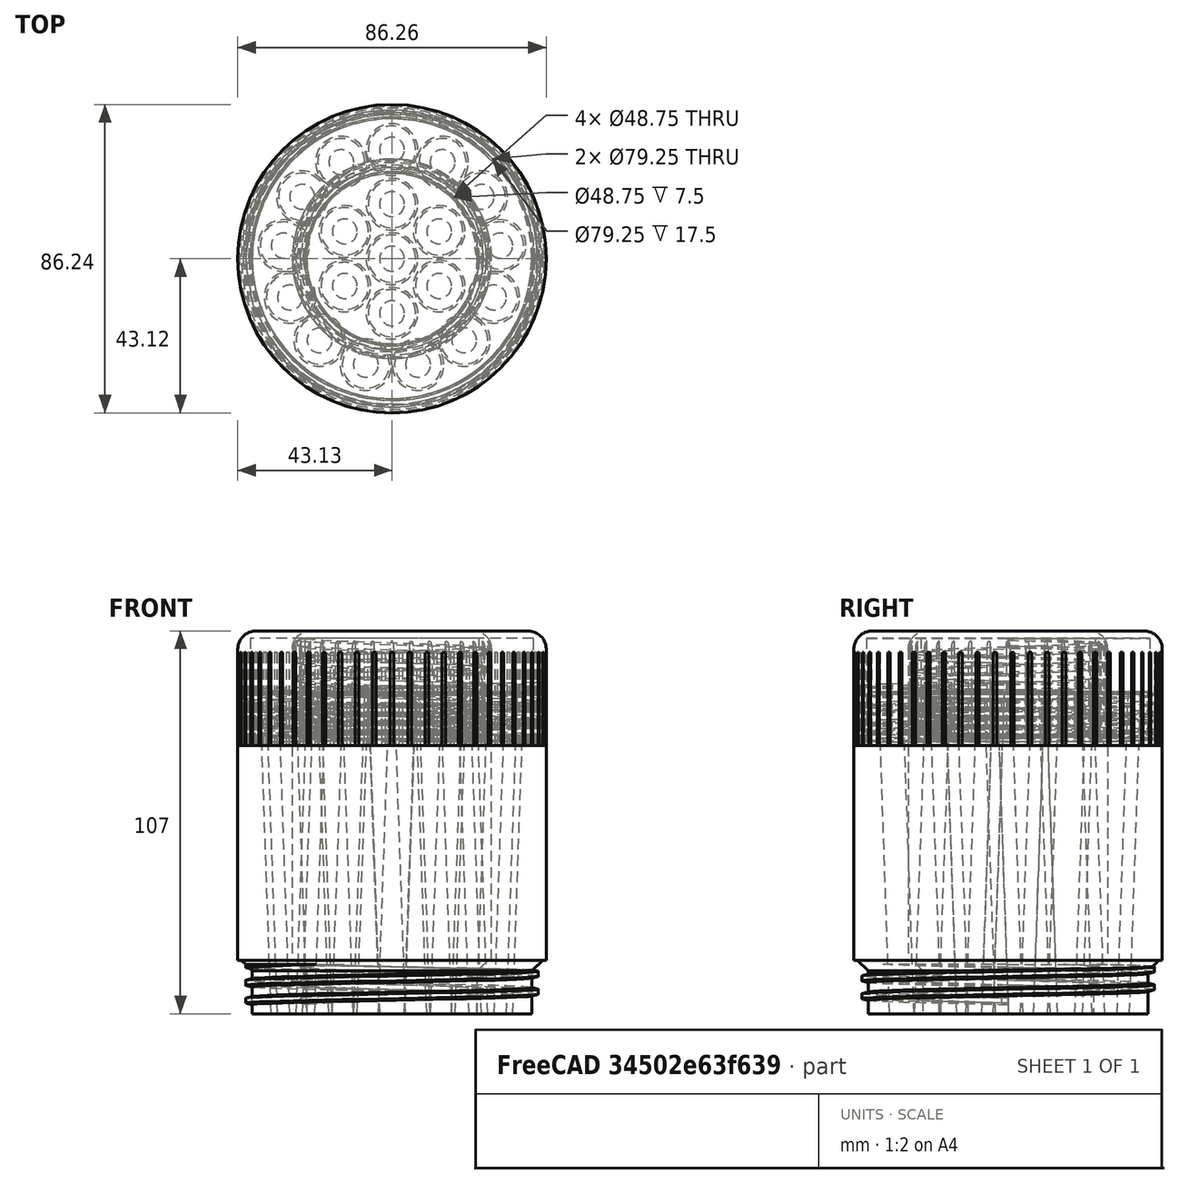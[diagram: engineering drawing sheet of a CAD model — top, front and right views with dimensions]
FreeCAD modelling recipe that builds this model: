
FCSTD DOCUMENT  (FreeCAD 2023.131R26244 +5365 (Git))
Label: Joint Holder
License: All rights reserved
LicenseURL: http://en.wikipedia.org/wiki/All_rights_reserved
objects: Sketcher::SketchObject×23, PartDesign::Pocket×13, PartDesign::Chamfer×6, PartDesign::PolarPattern×5, PartDesign::Pad×4, PartDesign::AdditiveHelix×4, PartDesign::Body×4, PartDesign::SubtractiveHelix×2, PartDesign::Fillet×2, Spreadsheet::Sheet×1
note: 158 computed .brp shape members not serialized (recipe doc carries the construction recipe); baked Part::Feature solids carry a one-line shape summary decoded from their .brp

FEATURE [Spreadsheet::Sheet] Spreadsheet  label="Parameters"
  PythonMode = false
  ShowCells = 0
  TreeRank = 1
  cells = A1=Thickness; B1(Thickness)=2; A2=Seven Cone Diameter; B2(small_holder_diameter)==Cone_Offset * 3 + Thickness * 5; D2=<-- Calculated; F2==large_holder_diameter / small_holder_diameter; A3=Twenty Holder Diameter; B3(large_holder_diameter)==Cone_Offset * 5 + Thickness * 5; D3=<-- Calculated; A4=Body Height; B4(body_height)=90; A5=Shoulder Height; B5(shoulder_height)=15; A6=Shoulder Depth; B6(shoulder_depth)==Thickness * 2; D6=<-- Calculated; A7=Cap Recess; B7(cap_recess)=15; A9=Cone Max Diameter; B9(Cone_Diameter_Max)=13.25; A10=Cone Min Diameter; B10(Cone_Diameter_Min)=6; A11=Cone Length; B11(Cone_Length)=110; A12=Cone Angle; B12(Cone_Angle)=2; E12==asin((Cone_Diameter_Max - Cone_Diameter_Min) / Cone_Length); A13=Cone Offset; B13(Cone_Offset)==Cone_Diameter_Max + Thickness; D13=<-- Calculated; A14=1st Cone Ring Count; B14(Cone_1st_Ring_Count)=6; A15=2nd Cone Ring Count; B15(Cone_2nd_Ring_Count)=13; A17=Tooth Depth; B17(tooth_depth)=2; A18=Thread Pitch; B18(thread_pitch)=2.5; A19=Thread Angle; B19(thread_angle)=15; A20=Thread Depth; B20(thread_depth)=2; A21=Thread Clearance; B21(thread_clearance)==thread_depth / 10
FEATURE [Sketcher::SketchObject] Sketch
  ArcFitTolerance = 1e-06
  AttachmentSupport = -> [XY_Plane]
  ExternalBSplineMaxDegree = 5
  ExternalBSplineTolerance = 0.0001
  FullyConstrained = true
  InternalTolerance = 1e-06
  InvalidShape = false
  MakeInternals = false
  MapMode = 5
  Support = -> [XY_Plane]
  TreeRank = 12
  ValidateShape = true
  expr: Constraints[1] = Spreadsheet.small_holder_diameter
  sketch-geometry (1):
    g0: Circle CenterX=0 CenterY=0 CenterZ=0 NormalX=0 NormalY=0 NormalZ=1 AngleXU=0 Radius=27.875
  constraints (2):
    c: Coincident(g0,g-1)
    c: Diameter(g0) = 55.75
FEATURE [PartDesign::Pad] Pad  label="Small Body"
  AddSubType = 0
  AlongSketchNormal = false
  AutoTaperInnerAngle = true
  CheckUpToFaceLimits = true
  ClaimChildren = false
  Direction = (0,0,1)
  Fit = 0
  FitJoin = 0
  InnerFit = 0
  InnerFitJoin = 0
  InvalidShape = false
  Length = 15
  Length2 = 75
  Linearize = true
  NewSolid = false
  Profile = -> Sketch
  Suppress = false
  TaperInnerAngle = 0
  TaperInnerAngleRev = 0
  TreeRank = 13
  Type = 4
  ValidateShape = true
  _ProfileBasedVersion = 1
  expr: Length = <<Parameters>>.shoulder_height
  expr: Length2 = <<Parameters>>.body_height - <<Parameters>>.shoulder_height
FEATURE [Sketcher::SketchObject] Sketch001
  ArcFitTolerance = 1e-06
  AttachmentSupport = -> [Pad]
  ExternalBSplineMaxDegree = 5
  ExternalBSplineTolerance = 0.0001
  FullyConstrained = true
  InternalTolerance = 1e-06
  InvalidShape = false
  MakeInternals = false
  MapMode = 5
  Placement = pos=(0,0,15) rot=(0,0,1;0rad)
  Support = -> [Pad]
  TreeRank = 14
  ValidateShape = true
  expr: Constraints[1] = <<Parameters>>.Cone_Diameter_Max
  sketch-geometry (1):
    g0: Circle CenterX=0 CenterY=0 CenterZ=0 NormalX=0 NormalY=0 NormalZ=1 AngleXU=0 Radius=6.625
  constraints (2):
    c: Coincident(g0,g-1)
    c: Diameter(g0) = 13.25
FEATURE [PartDesign::Pocket] Pocket  label="Small Middle Cone"
  AddSubType = 1
  AutoTaperInnerAngle = true
  BaseFeature = -> Pad
  CheckUpToFaceLimits = true
  ClaimChildren = false
  Fit = 0
  FitJoin = 0
  InnerFit = 0
  InnerFitJoin = 0
  InvalidShape = false
  Length = 110
  Length2 = 100
  Linearize = true
  NewSolid = false
  Profile = -> Sketch001
  Suppress = false
  TaperAngle = -2
  TaperInnerAngle = 2
  TaperInnerAngleRev = 0
  TreeRank = 15
  Type = 0
  ValidateShape = true
  _ProfileBasedVersion = 1
  _Version = 1
  expr: Length = <<Parameters>>.Cone_Length
  expr: TaperAngle = -<<Parameters>>.Cone_Angle
FEATURE [Sketcher::SketchObject] Sketch002
  ArcFitTolerance = 1e-06
  AttachmentSupport = -> [Pocket]
  ExternalBSplineMaxDegree = 5
  ExternalBSplineTolerance = 0.0001
  FullyConstrained = true
  InternalTolerance = 1e-06
  InvalidShape = false
  MakeInternals = false
  MapMode = 5
  Placement = pos=(0,0,15) rot=(0,0,1;0rad)
  Support = -> [Pocket]
  TreeRank = 16
  ValidateShape = true
  expr: Constraints[1] = <<Parameters>>.Cone_Diameter_Max
  expr: Constraints[2] = <<Parameters>>.Cone_Offset
  sketch-geometry (1):
    g0: Circle CenterX=0 CenterY=15.25 CenterZ=0 NormalX=0 NormalY=0 NormalZ=1 AngleXU=0 Radius=6.625
  constraints (3):
    c: PointOnObject(g0,g-2)
    c: Diameter(g0) = 13.25
    c: DistanceY(g-1,g0) = 15.25
FEATURE [PartDesign::Pocket] Pocket001  label="Small Outer Cone"
  AddSubType = 1
  AutoTaperInnerAngle = true
  BaseFeature = -> Pocket
  CheckUpToFaceLimits = true
  ClaimChildren = false
  Fit = 0
  FitJoin = 0
  InnerFit = 0
  InnerFitJoin = 0
  InvalidShape = false
  Length = 110
  Length2 = 100
  Linearize = true
  NewSolid = false
  Profile = -> Sketch002
  Suppress = false
  TaperAngle = -2
  TaperInnerAngle = 2
  TaperInnerAngleRev = 0
  TreeRank = 17
  Type = 0
  ValidateShape = true
  _ProfileBasedVersion = 1
  _Version = 1
  expr: Length = <<Parameters>>.Cone_Length
  expr: TaperAngle = -<<Parameters>>.Cone_Angle
FEATURE [PartDesign::PolarPattern] PolarPattern  label="Small Outer Cone Ring"
  AddSubType = 0
  Angle = 360
  Axis = -> Sketch002 [N_Axis]
  BaseFeature = -> Pocket001
  CopyShape = false
  InvalidShape = false
  NewSolid = false
  Occurrences = 6
  OriginalSubs = -> [Pocket001]
  Originals = -> [Pocket001]
  ParallelTransform = true
  SubTransform = true
  Suppress = false
  TreeRank = 18
  ValidateShape = true
  _Version = 3
  expr: Occurrences = <<Parameters>>.Cone_1st_Ring_Count
FEATURE [Sketcher::SketchObject] Sketch003
  ArcFitTolerance = 1e-06
  AttachmentSupport = -> [XY_Plane001]
  ExternalBSplineMaxDegree = 5
  ExternalBSplineTolerance = 0.0001
  FullyConstrained = true
  InternalTolerance = 1e-06
  InvalidShape = false
  MakeInternals = false
  MapMode = 5
  Support = -> [XY_Plane001]
  TreeRank = 29
  ValidateShape = true
  expr: Constraints[1] = <<Parameters>>.large_holder_diameter
  sketch-geometry (1):
    g0: Circle CenterX=0 CenterY=0 CenterZ=0 NormalX=0 NormalY=0 NormalZ=1 AngleXU=0 Radius=43.125
  constraints (2):
    c: Coincident(g0,g-1)
    c: Diameter(g0) = 86.25
FEATURE [PartDesign::Pad] Pad001  label="Large Body"
  AddSubType = 0
  AlongSketchNormal = false
  AutoTaperInnerAngle = true
  CheckUpToFaceLimits = true
  ClaimChildren = false
  Direction = (0,0,1)
  Fit = 0
  FitJoin = 0
  InnerFit = 0
  InnerFitJoin = 0
  InvalidShape = false
  Length = 15
  Length2 = 75
  Linearize = true
  NewSolid = false
  Profile = -> Sketch003
  Suppress = false
  TaperInnerAngle = 0
  TaperInnerAngleRev = 0
  TreeRank = 30
  Type = 4
  ValidateShape = true
  _ProfileBasedVersion = 1
  expr: Length = <<Parameters>>.shoulder_height
  expr: Length2 = <<Parameters>>.body_height - <<Parameters>>.shoulder_height
FEATURE [Sketcher::SketchObject] Sketch004
  ArcFitTolerance = 1e-06
  AttachmentSupport = -> [Pad001]
  ExternalBSplineMaxDegree = 5
  ExternalBSplineTolerance = 0.0001
  FullyConstrained = true
  InternalTolerance = 1e-06
  InvalidShape = false
  MakeInternals = false
  MapMode = 5
  Placement = pos=(0,0,15) rot=(0,0,1;0rad)
  Support = -> [Pad001]
  TreeRank = 31
  ValidateShape = true
  expr: Constraints[1] = <<Parameters>>.Cone_Diameter_Max
  sketch-geometry (1):
    g0: Circle CenterX=0 CenterY=0 CenterZ=0 NormalX=0 NormalY=0 NormalZ=1 AngleXU=0 Radius=6.625
  constraints (2):
    c: Coincident(g0,g-1)
    c: Diameter(g0) = 13.25
FEATURE [PartDesign::Pocket] Pocket002  label="Large Middle Cone"
  AddSubType = 1
  AutoTaperInnerAngle = true
  BaseFeature = -> Pad001
  CheckUpToFaceLimits = true
  ClaimChildren = false
  Fit = 0
  FitJoin = 0
  InnerFit = 0
  InnerFitJoin = 0
  InvalidShape = false
  Length = 110
  Length2 = 100
  Linearize = true
  NewSolid = false
  Profile = -> Sketch004
  Suppress = false
  TaperAngle = -2
  TaperInnerAngle = 2
  TaperInnerAngleRev = 0
  TreeRank = 32
  Type = 0
  ValidateShape = true
  _ProfileBasedVersion = 1
  _Version = 1
  expr: Length = <<Parameters>>.Cone_Length
  expr: TaperAngle = -<<Parameters>>.Cone_Angle
FEATURE [Sketcher::SketchObject] Sketch005
  ArcFitTolerance = 1e-06
  AttachmentSupport = -> [Pocket002]
  ExternalBSplineMaxDegree = 5
  ExternalBSplineTolerance = 0.0001
  FullyConstrained = true
  InternalTolerance = 1e-06
  InvalidShape = false
  MakeInternals = false
  MapMode = 5
  Placement = pos=(0,0,15) rot=(0,0,1;0rad)
  Support = -> [Pocket002]
  TreeRank = 33
  ValidateShape = true
  expr: Constraints[1] = <<Parameters>>.Cone_Diameter_Max
  expr: Constraints[2] = <<Parameters>>.Cone_Offset
  sketch-geometry (1):
    g0: Circle CenterX=0 CenterY=15.25 CenterZ=0 NormalX=0 NormalY=0 NormalZ=1 AngleXU=0 Radius=6.625
  constraints (3):
    c: PointOnObject(g0,g-2)
    c: Diameter(g0) = 13.25
    c: DistanceY(g-1,g0) = 15.25
FEATURE [PartDesign::Pocket] Pocket003  label="Large Inner Cone"
  AddSubType = 1
  AutoTaperInnerAngle = true
  BaseFeature = -> Pocket002
  CheckUpToFaceLimits = true
  ClaimChildren = false
  Fit = 0
  FitJoin = 0
  InnerFit = 0
  InnerFitJoin = 0
  InvalidShape = false
  Length = 110
  Length2 = 100
  Linearize = true
  NewSolid = false
  Profile = -> Sketch005
  Suppress = false
  TaperAngle = -2
  TaperInnerAngle = 2
  TaperInnerAngleRev = 0
  TreeRank = 34
  Type = 0
  ValidateShape = true
  _ProfileBasedVersion = 1
  _Version = 1
  expr: Length = <<Parameters>>.Cone_Length
  expr: TaperAngle = -<<Parameters>>.Cone_Angle
FEATURE [PartDesign::PolarPattern] PolarPattern001  label="Large Inner Cone Ring"
  AddSubType = 0
  Angle = 360
  Axis = -> Z_Axis001
  BaseFeature = -> Pocket003
  CopyShape = false
  InvalidShape = false
  NewSolid = false
  Occurrences = 6
  ParallelTransform = true
  SubTransform = true
  Suppress = false
  TreeRank = 35
  ValidateShape = true
  _Version = 3
  expr: Occurrences = <<Parameters>>.Cone_1st_Ring_Count
FEATURE [Sketcher::SketchObject] Sketch006
  ArcFitTolerance = 1e-06
  AttachmentSupport = -> [PolarPattern001]
  ExternalBSplineMaxDegree = 5
  ExternalBSplineTolerance = 0.0001
  FullyConstrained = true
  InternalTolerance = 1e-06
  InvalidShape = false
  MakeInternals = false
  MapMode = 5
  Placement = pos=(0,0,15) rot=(0,0,1;0rad)
  Support = -> [PolarPattern001]
  TreeRank = 36
  ValidateShape = true
  expr: Constraints[1] = <<Parameters>>.Cone_Diameter_Max
  expr: Constraints[2] = <<Parameters>>.Cone_Offset * 2
  sketch-geometry (1):
    g0: Circle CenterX=0 CenterY=30.5 CenterZ=0 NormalX=0 NormalY=0 NormalZ=1 AngleXU=0 Radius=6.625
  constraints (3):
    c: PointOnObject(g0,g-2)
    c: Diameter(g0) = 13.25
    c: DistanceY(g-1,g0) = 30.5
FEATURE [PartDesign::Pocket] Pocket004  label="Large Outer Cone"
  AddSubType = 1
  AutoTaperInnerAngle = true
  BaseFeature = -> PolarPattern001
  CheckUpToFaceLimits = true
  ClaimChildren = false
  Fit = 0
  FitJoin = 0
  InnerFit = 0
  InnerFitJoin = 0
  InvalidShape = false
  Length = 110
  Length2 = 100
  Linearize = true
  NewSolid = false
  Profile = -> Sketch006
  Suppress = false
  TaperAngle = -2
  TaperInnerAngle = 2
  TaperInnerAngleRev = 0
  TreeRank = 37
  Type = 0
  ValidateShape = true
  _ProfileBasedVersion = 1
  _Version = 1
  expr: Length = <<Parameters>>.Cone_Length
  expr: TaperAngle = -<<Parameters>>.Cone_Angle
FEATURE [PartDesign::PolarPattern] PolarPattern002  label="Large Outer Cone Ring"
  AddSubType = 0
  Angle = 360
  Axis = -> Sketch006 [N_Axis]
  BaseFeature = -> Pocket004
  CopyShape = false
  InvalidShape = false
  NewSolid = false
  Occurrences = 13
  OriginalSubs = -> [Pocket004]
  Originals = -> [Pocket004]
  ParallelTransform = true
  SubTransform = true
  Suppress = false
  TreeRank = 38
  ValidateShape = true
  _Version = 3
  expr: Occurrences = <<Parameters>>.Cone_2nd_Ring_Count
FEATURE [Sketcher::SketchObject] Sketch007
  ArcFitTolerance = 1e-06
  AttachmentSupport = -> [PolarPattern]
  ExternalBSplineMaxDegree = 5
  ExternalBSplineTolerance = 0.0001
  FullyConstrained = true
  InternalTolerance = 1e-06
  InvalidShape = false
  MakeInternals = false
  MapMode = 5
  Placement = pos=(0,0,15) rot=(0,0,1;0rad)
  Support = -> [PolarPattern]
  TreeRank = 39
  ValidateShape = true
  expr: Constraints[2] = <<Parameters>>.small_holder_diameter * 2
  expr: Constraints[3] = <<Parameters>>.small_holder_diameter - 2 * <<Parameters>>.shoulder_depth
  sketch-geometry (2):
    g0: Circle CenterX=0 CenterY=0 CenterZ=0 NormalX=0 NormalY=0 NormalZ=1 AngleXU=0 Radius=23.875
    g1: Circle CenterX=0 CenterY=0 CenterZ=0 NormalX=0 NormalY=0 NormalZ=1 AngleXU=0 Radius=55.75
  constraints (4):
    c: Coincident(g0,g-1)
    c: Coincident(g1,g0)
    c: Diameter(g1) = 111.5
    c: Diameter(g0) = 47.75
FEATURE [PartDesign::Pocket] Pocket005  label="Small Top Shoulder"
  AddSubType = 1
  AutoTaperInnerAngle = true
  BaseFeature = -> PolarPattern
  CheckUpToFaceLimits = true
  ClaimChildren = false
  Fit = 0
  FitJoin = 0
  InnerFit = 0
  InnerFitJoin = 0
  InvalidShape = false
  Length = 15
  Length2 = 100
  Linearize = true
  NewSolid = false
  Profile = -> Sketch007
  Suppress = false
  TaperInnerAngle = 0
  TaperInnerAngleRev = 0
  TreeRank = 40
  Type = 0
  ValidateShape = true
  _ProfileBasedVersion = 1
  _Version = 1
  expr: Length = <<Parameters>>.shoulder_height
FEATURE [Sketcher::SketchObject] Sketch008
  ArcFitTolerance = 1e-06
  AttachmentSupport = -> [Pocket005]
  ExternalBSplineMaxDegree = 5
  ExternalBSplineTolerance = 0.0001
  FullyConstrained = true
  InternalTolerance = 1e-06
  InvalidShape = false
  MakeInternals = false
  MapMode = 5
  Placement = pos=(0,0,-75) rot=(1,0,0;3.14159rad)
  Support = -> [Pocket005]
  TreeRank = 41
  ValidateShape = true
  expr: Constraints[1] = <<Parameters>>.small_holder_diameter * 2
  expr: Constraints[3] = <<Parameters>>.small_holder_diameter - 2 * <<Parameters>>.shoulder_depth
  sketch-geometry (2):
    g0: Circle CenterX=0 CenterY=0 CenterZ=0 NormalX=0 NormalY=0 NormalZ=1 AngleXU=0 Radius=55.75
    g1: Circle CenterX=0 CenterY=0 CenterZ=0 NormalX=0 NormalY=0 NormalZ=1 AngleXU=0 Radius=23.875
  constraints (4):
    c: Coincident(g0,g-1)
    c: Diameter(g0) = 111.5
    c: Coincident(g1,g0)
    c: Diameter(g1) = 47.75
FEATURE [PartDesign::Pocket] Pocket006  label="Small Bottom Shoulder"
  AddSubType = 1
  AutoTaperInnerAngle = true
  BaseFeature = -> Pocket005
  CheckUpToFaceLimits = true
  ClaimChildren = false
  Fit = 0
  FitJoin = 0
  InnerFit = 0
  InnerFitJoin = 0
  InvalidShape = false
  Length = 15
  Length2 = 100
  Linearize = true
  NewSolid = false
  Profile = -> Sketch008
  Suppress = false
  TaperInnerAngle = 0
  TaperInnerAngleRev = 0
  TreeRank = 42
  Type = 0
  ValidateShape = true
  _ProfileBasedVersion = 1
  _Version = 1
  expr: Length = <<Parameters>>.shoulder_height
FEATURE [Sketcher::SketchObject] Sketch011
  ArcFitTolerance = 1e-06
  AttachmentSupport = -> [PolarPattern002]
  ExternalBSplineMaxDegree = 5
  ExternalBSplineTolerance = 0.0001
  FullyConstrained = true
  InternalTolerance = 1e-06
  InvalidShape = false
  MakeInternals = false
  MapMode = 5
  Placement = pos=(0,0,15) rot=(0,0,1;0rad)
  Support = -> [PolarPattern002]
  TreeRank = 49
  ValidateShape = true
  expr: Constraints[2] = <<Parameters>>.large_holder_diameter - 2 * <<Parameters>>.shoulder_depth
  expr: Constraints[3] = <<Parameters>>.large_holder_diameter * 2
  sketch-geometry (2):
    g0: Circle CenterX=0 CenterY=0 CenterZ=0 NormalX=0 NormalY=0 NormalZ=1 AngleXU=0 Radius=39.125
    g1: Circle CenterX=0 CenterY=0 CenterZ=0 NormalX=0 NormalY=0 NormalZ=1 AngleXU=0 Radius=86.25
  constraints (4):
    c: Coincident(g0,g-1)
    c: Coincident(g1,g0)
    c: Diameter(g0) = 78.25
    c: Diameter(g1) = 172.5
FEATURE [PartDesign::Pocket] Pocket007  label="Large Top Shoulder"
  AddSubType = 1
  AutoTaperInnerAngle = true
  BaseFeature = -> PolarPattern002
  CheckUpToFaceLimits = true
  ClaimChildren = false
  Fit = 0
  FitJoin = 0
  InnerFit = 0
  InnerFitJoin = 0
  InvalidShape = false
  Length = 15
  Length2 = 100
  Linearize = true
  NewSolid = false
  Profile = -> Sketch011
  Suppress = false
  TaperInnerAngle = 0
  TaperInnerAngleRev = 0
  TreeRank = 50
  Type = 0
  ValidateShape = true
  _ProfileBasedVersion = 1
  _Version = 1
  expr: Length = <<Parameters>>.shoulder_height
FEATURE [Sketcher::SketchObject] Sketch012
  ArcFitTolerance = 1e-06
  AttachmentSupport = -> [Pocket007]
  ExternalBSplineMaxDegree = 5
  ExternalBSplineTolerance = 0.0001
  FullyConstrained = true
  InternalTolerance = 1e-06
  InvalidShape = false
  MakeInternals = false
  MapMode = 5
  Placement = pos=(0,0,-75) rot=(1,0,0;3.14159rad)
  Support = -> [Pocket007]
  TreeRank = 51
  ValidateShape = true
  expr: Constraints[2] = <<Parameters>>.large_holder_diameter - 2 * <<Parameters>>.shoulder_depth
  expr: Constraints[3] = <<Parameters>>.large_holder_diameter * 2
  sketch-geometry (2):
    g0: Circle CenterX=0 CenterY=0 CenterZ=0 NormalX=0 NormalY=0 NormalZ=1 AngleXU=0 Radius=39.125
    g1: Circle CenterX=0 CenterY=0 CenterZ=0 NormalX=0 NormalY=0 NormalZ=1 AngleXU=0 Radius=86.25
  constraints (4):
    c: Coincident(g0,g-1)
    c: Coincident(g1,g0)
    c: Diameter(g0) = 78.25
    c: Diameter(g1) = 172.5
FEATURE [PartDesign::Pocket] Pocket008  label="Large Bottom Shoulder"
  AddSubType = 1
  AutoTaperInnerAngle = true
  BaseFeature = -> Pocket007
  CheckUpToFaceLimits = true
  ClaimChildren = false
  Fit = 0
  FitJoin = 0
  InnerFit = 0
  InnerFitJoin = 0
  InvalidShape = false
  Length = 15
  Length2 = 100
  Linearize = true
  NewSolid = false
  Profile = -> Sketch012
  Suppress = false
  TaperInnerAngle = 0
  TaperInnerAngleRev = 0
  TreeRank = 52
  Type = 0
  ValidateShape = true
  _ProfileBasedVersion = 1
  _Version = 1
  expr: Length = <<Parameters>>.shoulder_height
FEATURE [Sketcher::SketchObject] Sketch013
  ArcFitTolerance = 1e-06
  AttachmentSupport = -> [XZ_Plane001]
  ExternalBSplineMaxDegree = 5
  ExternalBSplineTolerance = 0.0001
  FullyConstrained = true
  InternalTolerance = 1e-06
  InvalidShape = false
  MakeInternals = false
  MapMode = 5
  Placement = pos=(0,0,0) rot=(1,0,0;1.5708rad)
  Support = -> [XZ_Plane001]
  TreeRank = 53
  ValidateShape = true
  expr: Constraints[10] = (<<Parameters>>.large_holder_diameter - 2 * <<Parameters>>.shoulder_depth) / 2
  expr: Constraints[11] = 90 - <<Parameters>>.thread_angle
  expr: Constraints[6] = 90 - <<Parameters>>.thread_angle
  expr: Constraints[7] = <<Parameters>>.thread_pitch - <<Parameters>>.thread_clearance
  expr: Constraints[8] = <<Parameters>>.thread_depth - <<Parameters>>.thread_clearance
  sketch-geometry (4):
    g0: LineSegment StartX=-39.125 StartY=0 StartZ=0 EndX=-39.125 EndY=-2.3 EndZ=0
    g1: LineSegment StartX=-40.925 StartY=-0.482309 StartZ=0 EndX=-40.925 EndY=-1.81769 EndZ=0
    g2: LineSegment StartX=-40.925 StartY=-0.482309 StartZ=0 EndX=-39.125 EndY=-1e-16 EndZ=0
    g3: LineSegment StartX=-40.925 StartY=-1.81769 StartZ=0 EndX=-39.125 EndY=-2.3 EndZ=0
  constraints (12):
    c: Vertical(g0)
    c: Vertical(g1)
    c: Coincident(g2,g1)
    c: Coincident(g2,g0)
    c: Coincident(g3,g1)
    c: Coincident(g3,g0)
    c: Angle(g0,g3) = 1.309
    c: DistanceY(g0,g0) = 2.3
    c: DistanceX(g1,g0) = 1.8
    c: DistanceY(g0,g-1) = 0
    c: DistanceX(g0,g-1) = 39.125
    c: Angle(g2,g0) = 1.309
FEATURE [Sketcher::SketchObject] Sketch014
  ArcFitTolerance = 1e-06
  AttachmentSupport = -> [XZ_Plane001]
  ExternalBSplineMaxDegree = 5
  ExternalBSplineTolerance = 0.0001
  FullyConstrained = true
  InternalTolerance = 1e-06
  InvalidShape = false
  MakeInternals = false
  MapMode = 5
  Placement = pos=(0,0,0) rot=(1,0,0;1.5708rad)
  Support = -> [XZ_Plane001]
  TreeRank = 55
  ValidateShape = true
  expr: Constraints[10] = <<Parameters>>.body_height - <<Parameters>>.shoulder_height - <<Parameters>>.thread_pitch
  expr: Constraints[11] = 90 - <<Parameters>>.thread_angle
  expr: Constraints[6] = 90 - <<Parameters>>.thread_angle
  expr: Constraints[7] = <<Parameters>>.thread_pitch - <<Parameters>>.thread_clearance
  expr: Constraints[8] = <<Parameters>>.thread_depth - <<Parameters>>.thread_clearance
  expr: Constraints[9] = (<<Parameters>>.large_holder_diameter - 2 * <<Parameters>>.shoulder_depth) / 2
  sketch-geometry (4):
    g0: LineSegment StartX=-39.125 StartY=-72.5 StartZ=0 EndX=-39.125 EndY=-70.2 EndZ=0
    g1: LineSegment StartX=-40.925 StartY=-72.0177 StartZ=0 EndX=-40.925 EndY=-70.6823 EndZ=0
    g2: LineSegment StartX=-40.925 StartY=-70.6823 StartZ=0 EndX=-39.125 EndY=-70.2 EndZ=0
    g3: LineSegment StartX=-40.925 StartY=-72.0177 StartZ=0 EndX=-39.125 EndY=-72.5 EndZ=0
  constraints (12):
    c: Vertical(g0)
    c: Vertical(g1)
    c: Coincident(g2,g1)
    c: Coincident(g2,g0)
    c: Coincident(g3,g1)
    c: Coincident(g3,g0)
    c: Angle(g0,g3) = 1.309
    c: DistanceY(g0,g0) = 2.3
    c: DistanceX(g1,g0) = 1.8
    c: DistanceX(g0,g-1) = 39.125
    c: DistanceY(g0,g-1) = 72.5
    c: Angle(g2,g0) = 1.309
FEATURE [Sketcher::SketchObject] Sketch015
  ArcFitTolerance = 1e-06
  AttachmentSupport = -> [XY_Plane002]
  ExternalBSplineMaxDegree = 5
  ExternalBSplineTolerance = 0.0001
  FullyConstrained = true
  InternalTolerance = 1e-06
  InvalidShape = false
  MakeInternals = false
  MapMode = 5
  Support = -> [XY_Plane002]
  TreeRank = 68
  ValidateShape = true
  expr: Constraints[1] = <<Parameters>>.small_holder_diameter
  sketch-geometry (1):
    g0: Circle CenterX=0 CenterY=0 CenterZ=0 NormalX=0 NormalY=0 NormalZ=1 AngleXU=0 Radius=27.875
  constraints (2):
    c: Coincident(g0,g-1)
    c: Diameter(g0) = 55.75
FEATURE [PartDesign::Pad] Pad002  label="Small Cap Body"
  AddSubType = 0
  AlongSketchNormal = false
  AutoTaperInnerAngle = true
  CheckUpToFaceLimits = true
  ClaimChildren = false
  Direction = (0,0,1)
  Fit = 0
  FitJoin = 0
  InnerFit = 0
  InnerFitJoin = 0
  InvalidShape = false
  Length = 32
  Length2 = 100
  Linearize = true
  NewSolid = false
  Profile = -> Sketch015
  Suppress = false
  TaperInnerAngle = 0
  TaperInnerAngleRev = 0
  TreeRank = 69
  Type = 0
  ValidateShape = true
  _ProfileBasedVersion = 1
  expr: Length = <<Parameters>>.shoulder_height + <<Parameters>>.cap_recess + <<Parameters>>.Thickness
FEATURE [Sketcher::SketchObject] Sketch016
  ArcFitTolerance = 1e-06
  AttachmentSupport = -> [Pad002]
  ExternalBSplineMaxDegree = 5
  ExternalBSplineTolerance = 0.0001
  FullyConstrained = true
  InternalTolerance = 1e-06
  InvalidShape = false
  MakeInternals = false
  MapMode = 5
  Placement = pos=(0,0,0) rot=(1,0,0;3.14159rad)
  Support = -> [Pad002]
  TreeRank = 70
  ValidateShape = true
  expr: Constraints[1] = <<Parameters>>.small_holder_diameter - 2 * <<Parameters>>.shoulder_depth + 1
  sketch-geometry (1):
    g0: Circle CenterX=0 CenterY=0 CenterZ=0 NormalX=0 NormalY=0 NormalZ=1 AngleXU=0 Radius=24.375
  constraints (2):
    c: Coincident(g0,g-1)
    c: Diameter(g0) = 48.75
FEATURE [PartDesign::Pocket] Pocket009  label="Small Shoulder Recess"
  AddSubType = 1
  AutoTaperInnerAngle = true
  BaseFeature = -> Pad002
  CheckUpToFaceLimits = true
  ClaimChildren = false
  Fit = 0
  FitJoin = 0
  InnerFit = 0
  InnerFitJoin = 0
  InvalidShape = false
  Length = 30
  Length2 = 100
  Linearize = true
  NewSolid = false
  Profile = -> Sketch016
  Suppress = false
  TaperInnerAngle = 0
  TaperInnerAngleRev = 0
  TreeRank = 71
  Type = 0
  ValidateShape = true
  _ProfileBasedVersion = 1
  _Version = 1
  expr: Length = <<Parameters>>.shoulder_height + <<Parameters>>.cap_recess
FEATURE [Sketcher::SketchObject] Sketch019
  ArcFitTolerance = 1e-06
  AttachmentSupport = -> [XY_Plane003]
  ExternalBSplineMaxDegree = 5
  ExternalBSplineTolerance = 0.0001
  FullyConstrained = true
  InternalTolerance = 1e-06
  InvalidShape = false
  MakeInternals = false
  MapMode = 5
  Support = -> [XY_Plane003]
  TreeRank = 68
  ValidateShape = true
  expr: Constraints[1] = <<Parameters>>.large_holder_diameter
  sketch-geometry (1):
    g0: Circle CenterX=0 CenterY=0 CenterZ=0 NormalX=0 NormalY=0 NormalZ=1 AngleXU=0 Radius=43.125
  constraints (2):
    c: Coincident(g0,g-1)
    c: Diameter(g0) = 86.25
FEATURE [PartDesign::Pad] Pad003  label="Large Cap Body"
  AddSubType = 0
  AlongSketchNormal = false
  AutoTaperInnerAngle = true
  CheckUpToFaceLimits = true
  ClaimChildren = false
  Direction = (0,0,1)
  Fit = 0
  FitJoin = 0
  InnerFit = 0
  InnerFitJoin = 0
  InvalidShape = false
  Length = 32
  Length2 = 100
  Linearize = true
  NewSolid = false
  Profile = -> Sketch019
  Suppress = false
  TaperInnerAngle = 0
  TaperInnerAngleRev = 0
  TreeRank = 69
  Type = 0
  ValidateShape = true
  _ProfileBasedVersion = 1
  expr: Length = <<Parameters>>.shoulder_height + <<Parameters>>.cap_recess + <<Parameters>>.Thickness
FEATURE [Sketcher::SketchObject] Sketch020
  ArcFitTolerance = 1e-06
  AttachmentSupport = -> [Pad003]
  ExternalBSplineMaxDegree = 5
  ExternalBSplineTolerance = 0.0001
  FullyConstrained = true
  InternalTolerance = 1e-06
  InvalidShape = false
  MakeInternals = false
  MapMode = 5
  Placement = pos=(0,0,0) rot=(1,0,0;3.14159rad)
  Support = -> [Pad003]
  TreeRank = 70
  ValidateShape = true
  expr: Constraints[1] = <<Parameters>>.large_holder_diameter - 2 * <<Parameters>>.shoulder_depth + 1
  sketch-geometry (1):
    g0: Circle CenterX=0 CenterY=0 CenterZ=0 NormalX=0 NormalY=0 NormalZ=1 AngleXU=0 Radius=39.625
  constraints (2):
    c: Coincident(g0,g-1)
    c: Diameter(g0) = 79.25
FEATURE [PartDesign::Pocket] Pocket011  label="Large Shoulder Recess"
  AddSubType = 1
  AutoTaperInnerAngle = true
  BaseFeature = -> Pad003
  CheckUpToFaceLimits = true
  ClaimChildren = false
  Fit = 0
  FitJoin = 0
  InnerFit = 0
  InnerFitJoin = 0
  InvalidShape = false
  Length = 30
  Length2 = 100
  Linearize = true
  NewSolid = false
  Profile = -> Sketch020
  Suppress = false
  TaperInnerAngle = 0
  TaperInnerAngleRev = 0
  TreeRank = 71
  Type = 0
  ValidateShape = true
  _ProfileBasedVersion = 1
  _Version = 1
  expr: Length = <<Parameters>>.shoulder_height + <<Parameters>>.cap_recess
FEATURE [Sketcher::SketchObject] Sketch022
  ArcFitTolerance = 1e-06
  AttachmentSupport = -> [XZ_Plane003]
  ExternalBSplineMaxDegree = 5
  ExternalBSplineTolerance = 0.0001
  FullyConstrained = true
  InternalTolerance = 1e-06
  InvalidShape = false
  MakeInternals = false
  MapMode = 5
  Placement = pos=(0,0,0) rot=(1,0,0;1.5708rad)
  Support = -> [XZ_Plane003]
  TreeRank = 75
  ValidateShape = true
  expr: Constraints[11] = (<<Parameters>>.large_holder_diameter - 2 * <<Parameters>>.shoulder_depth + 1) / 2
  expr: Constraints[7] = <<Parameters>>.thread_depth
  expr: Constraints[8] = <<Parameters>>.thread_pitch
  expr: Constraints[9] = 90 - <<Parameters>>.thread_angle
  sketch-geometry (4):
    g0: LineSegment StartX=-39.625 StartY=-2.5 StartZ=0 EndX=-39.625 EndY=0 EndZ=0
    g1: LineSegment StartX=-41.625 StartY=-1.9641 StartZ=0 EndX=-41.625 EndY=0.535898 EndZ=0
    g2: LineSegment StartX=-41.625 StartY=0.535898 StartZ=0 EndX=-39.625 EndY=0 EndZ=0
    g3: LineSegment StartX=-41.625 StartY=-1.9641 StartZ=0 EndX=-39.625 EndY=-2.5 EndZ=0
  constraints (12):
    c: Vertical(g0)
    c: Vertical(g1)
    c: Coincident(g2,g1)
    c: Coincident(g2,g0)
    c: Coincident(g3,g1)
    c: Coincident(g3,g0)
    c: Equal(g2,g3)
    c: DistanceX(g1,g0) = 2
    c: DistanceY(g0,g0) = 2.5
    c: Angle(g0,g3) = 1.309
    c: DistanceY(g0,g-1) = 0
    c: DistanceX(g0,g-1) = 39.625
FEATURE [PartDesign::Chamfer] Chamfer  label="Small Shoulder Chamfer"
  AddSubType = 0
  Angle = 45
  Base = -> Pocket006 [Edge5,Edge4]
  BaseFeature = -> Pocket006
  ChamferType = 0
  FlipDirection = false
  InvalidShape = false
  NewSolid = false
  Size = 3
  Size2 = 1
  SupportTransform = false
  Suppress = false
  TreeRank = 89
  ValidateShape = true
  expr: Size = <<Parameters>>.shoulder_depth - 1
FEATURE [Sketcher::SketchObject] Sketch025
  ArcFitTolerance = 1e-06
  AttachmentSupport = -> [XZ_Plane]
  ExternalBSplineMaxDegree = 5
  ExternalBSplineTolerance = 0.0001
  FullyConstrained = true
  InternalTolerance = 1e-06
  InvalidShape = false
  MakeInternals = false
  MapMode = 5
  Placement = pos=(0,0,0) rot=(1,0,0;1.5708rad)
  Support = -> [XZ_Plane]
  TreeRank = 90
  ValidateShape = true
  expr: Constraints[10] = (<<Parameters>>.small_holder_diameter - 2 * <<Parameters>>.shoulder_depth) / 2
  expr: Constraints[11] = <<Parameters>>.shoulder_height - <<Parameters>>.thread_pitch
  expr: Constraints[6] = 90 - <<Parameters>>.thread_angle
  expr: Constraints[7] = 90 - <<Parameters>>.thread_angle
  expr: Constraints[8] = <<Parameters>>.thread_depth - <<Parameters>>.thread_clearance
  expr: Constraints[9] = <<Parameters>>.thread_pitch - <<Parameters>>.thread_clearance
  sketch-geometry (4):
    g0: LineSegment StartX=-23.875 StartY=12.5 StartZ=0 EndX=-23.875 EndY=10.2 EndZ=0
    g1: LineSegment StartX=-25.675 StartY=12.0177 StartZ=0 EndX=-25.675 EndY=10.6823 EndZ=0
    g2: LineSegment StartX=-25.675 StartY=12.0177 StartZ=0 EndX=-23.875 EndY=12.5 EndZ=0
    g3: LineSegment StartX=-25.675 StartY=10.6823 StartZ=0 EndX=-23.875 EndY=10.2 EndZ=0
  constraints (12):
    c: Vertical(g0)
    c: Vertical(g1)
    c: Coincident(g2,g1)
    c: Coincident(g2,g0)
    c: Coincident(g3,g1)
    c: Coincident(g3,g0)
    c: Angle(g2,g0) = 1.309
    c: Angle(g0,g3) = 1.309
    c: DistanceX(g1,g0) = 1.8
    c: DistanceY(g0,g0) = 2.3
    c: DistanceX(g0,g-1) = 23.875
    c: DistanceY(g-1,g0) = 12.5
FEATURE [PartDesign::AdditiveHelix] Helix  label="Small Top Threads"
  AddSubType = 0
  Angle = 0
  Axis = (0,-2e-16,1)
  Base = (0,0,0)
  BaseFeature = -> Chamfer
  ClaimChildren = false
  Fit = 0
  FitJoin = 0
  Growth = 0
  HasBeenEdited = true
  Height = 15
  InnerFit = 0
  InnerFitJoin = 0
  InvalidShape = false
  LeftHanded = false
  Linearize = true
  Mode = 0
  NewSolid = false
  Outside = false
  Pitch = 5
  Profile = -> Sketch025
  ReferenceAxis = -> Sketch025 [V_Axis]
  Reversed = true
  Suppress = false
  TreeRank = 91
  Turns = 3
  ValidateShape = true
  _ProfileBasedVersion = 1
  expr: Height = <<Parameters>>.shoulder_height
  expr: Pitch = <<Parameters>>.thread_pitch * 2
FEATURE [Sketcher::SketchObject] Sketch026
  ArcFitTolerance = 1e-06
  AttachmentSupport = -> [XZ_Plane]
  ExternalBSplineMaxDegree = 5
  ExternalBSplineTolerance = 0.0001
  FullyConstrained = true
  InternalTolerance = 1e-06
  InvalidShape = false
  MakeInternals = false
  MapMode = 5
  Placement = pos=(0,0,0) rot=(1,0,0;1.5708rad)
  Support = -> [XZ_Plane]
  TreeRank = 92
  ValidateShape = true
  expr: Constraints[10] = (<<Parameters>>.small_holder_diameter - 2 * <<Parameters>>.shoulder_depth) / 2
  expr: Constraints[11] = <<Parameters>>.body_height - <<Parameters>>.shoulder_height - <<Parameters>>.thread_pitch
  expr: Constraints[6] = 90 - <<Parameters>>.thread_angle
  expr: Constraints[7] = 90 - <<Parameters>>.thread_angle
  expr: Constraints[8] = <<Parameters>>.thread_depth - <<Parameters>>.thread_clearance
  expr: Constraints[9] = <<Parameters>>.thread_pitch - <<Parameters>>.thread_clearance
  sketch-geometry (4):
    g0: LineSegment StartX=-23.875 StartY=-72.5 StartZ=0 EndX=-23.875 EndY=-70.2 EndZ=0
    g1: LineSegment StartX=-25.675 StartY=-72.0177 StartZ=0 EndX=-25.675 EndY=-70.6823 EndZ=0
    g2: LineSegment StartX=-25.675 StartY=-70.6823 StartZ=0 EndX=-23.875 EndY=-70.2 EndZ=0
    g3: LineSegment StartX=-25.675 StartY=-72.0177 StartZ=0 EndX=-23.875 EndY=-72.5 EndZ=0
  constraints (12):
    c: Vertical(g0)
    c: Vertical(g1)
    c: Coincident(g2,g1)
    c: Coincident(g2,g0)
    c: Coincident(g3,g1)
    c: Coincident(g3,g0)
    c: Angle(g2,g0) = 1.309
    c: Angle(g0,g3) = 1.309
    c: DistanceX(g1,g0) = 1.8
    c: DistanceY(g0,g0) = 2.3
    c: DistanceX(g0,g-1) = 23.875
    c: DistanceY(g0,g-1) = 72.5
FEATURE [PartDesign::AdditiveHelix] Helix006  label="Small Bottom Threads"
  AddSubType = 0
  Angle = 0
  Axis = (0,-2e-16,1)
  Base = (0,0,0)
  BaseFeature = -> Helix
  ClaimChildren = false
  Fit = 0
  FitJoin = 0
  Growth = 0
  HasBeenEdited = true
  Height = 15
  InnerFit = 0
  InnerFitJoin = 0
  InvalidShape = false
  LeftHanded = false
  Linearize = true
  Mode = 0
  NewSolid = false
  Outside = false
  Pitch = 5
  Profile = -> Sketch026
  ReferenceAxis = -> Sketch026 [V_Axis]
  Suppress = false
  TreeRank = 93
  Turns = 3
  ValidateShape = true
  _ProfileBasedVersion = 1
  expr: Height = <<Parameters>>.shoulder_height
  expr: Pitch = <<Parameters>>.thread_pitch * 2
FEATURE [PartDesign::Body] Body  label="Seven Cone Body"
  AutoGroupSolids = false
  ClaimAllChildren = false
  ExportMode = 0
  Group = -> [Sketch,Pad,Sketch001,Pocket,Sketch002,Pocket001,PolarPattern,Sketch007,Pocket005,Sketch008,Pocket006,Chamfer,Sketch025,Helix,Sketch026,Helix006]
  InvalidShape = false
  Origin = -> Origin
  Tip = -> Helix006
  TreeRank = 11
  ValidateShape = true
  _ExportChildren = -> [Pad,Pocket,Pocket001,PolarPattern,Pocket005,Pocket006,Chamfer,Helix,Helix006]
  _GroupVersion = 1
FEATURE [PartDesign::Chamfer] Chamfer004
  AddSubType = 0
  Angle = 45
  Base = -> Pocket009 [Edge4]
  BaseFeature = -> Pocket009
  ChamferType = 0
  FlipDirection = false
  InvalidShape = false
  NewSolid = false
  Size = 3
  Size2 = 1
  SupportTransform = false
  Suppress = false
  TreeRank = 94
  ValidateShape = true
  expr: Size = <<Parameters>>.shoulder_depth - 1
FEATURE [Sketcher::SketchObject] Sketch027
  ArcFitTolerance = 1e-06
  AttachmentSupport = -> [XZ_Plane002]
  ExternalBSplineMaxDegree = 5
  ExternalBSplineTolerance = 0.0001
  FullyConstrained = true
  InternalTolerance = 1e-06
  InvalidShape = false
  MakeInternals = false
  MapMode = 5
  Placement = pos=(0,0,0) rot=(1,0,0;1.5708rad)
  Support = -> [XZ_Plane002]
  TreeRank = 95
  ValidateShape = true
  expr: Constraints[10] = <<Parameters>>.thread_depth
  expr: Constraints[11] = (<<Parameters>>.small_holder_diameter - 2 * <<Parameters>>.shoulder_depth + 1) / 2
  expr: Constraints[6] = <<Parameters>>.shoulder_height + <<Parameters>>.cap_recess
  expr: Constraints[7] = 90 - <<Parameters>>.thread_angle
  expr: Constraints[8] = 90 - <<Parameters>>.thread_angle
  expr: Constraints[9] = <<Parameters>>.thread_pitch
  sketch-geometry (4):
    g0: LineSegment StartX=-24.375 StartY=30 StartZ=0 EndX=-24.375 EndY=27.5 EndZ=0
    g1: LineSegment StartX=-26.375 StartY=29.4641 StartZ=0 EndX=-26.375 EndY=28.0359 EndZ=0
    g2: LineSegment StartX=-26.375 StartY=28.0359 StartZ=0 EndX=-24.375 EndY=27.5 EndZ=0
    g3: LineSegment StartX=-26.375 StartY=29.4641 StartZ=0 EndX=-24.375 EndY=30 EndZ=0
  constraints (12):
    c: Vertical(g0)
    c: Vertical(g1)
    c: Coincident(g2,g1)
    c: Coincident(g2,g0)
    c: Coincident(g3,g1)
    c: Coincident(g3,g0)
    c: DistanceY(g-1,g0) = 30
    c: Angle(g3,g0) = 1.309
    c: Angle(g0,g2) = 1.309
    c: DistanceY(g0,g0) = 2.5
    c: DistanceX(g1,g0) = 2
    c: DistanceX(g0,g-1) = 24.375
FEATURE [PartDesign::SubtractiveHelix] Helix007
  AddSubType = 1
  Angle = 0
  Axis = (0,-2e-16,1)
  Base = (0,0,0)
  BaseFeature = -> Chamfer004
  ClaimChildren = false
  Fit = 0
  FitJoin = 0
  Growth = 0
  HasBeenEdited = true
  Height = 30
  InnerFit = 0
  InnerFitJoin = 0
  InvalidShape = false
  LeftHanded = false
  Linearize = true
  Mode = 0
  NewSolid = false
  Outside = false
  Pitch = 5
  Profile = -> Sketch027
  ReferenceAxis = -> Sketch027 [V_Axis]
  Reversed = true
  Suppress = false
  TreeRank = 96
  Turns = 6
  ValidateShape = true
  _ProfileBasedVersion = 1
  expr: Height = <<Parameters>>.shoulder_height + <<Parameters>>.cap_recess
  expr: Pitch = <<Parameters>>.thread_pitch * 2
FEATURE [PartDesign::Fillet] Fillet
  AddSubType = 0
  Base = -> Helix007 [Edge12]
  BaseFeature = -> Helix007
  InvalidShape = false
  NewSolid = false
  Radius = 5
  SupportTransform = false
  Suppress = false
  TreeRank = 97
  ValidateShape = true
FEATURE [Sketcher::SketchObject] Sketch028
  ArcFitTolerance = 1e-06
  AttachmentSupport = -> [Fillet]
  ExternalBSplineMaxDegree = 5
  ExternalBSplineTolerance = 0.0001
  FullyConstrained = true
  InternalTolerance = 1e-06
  InvalidShape = false
  MakeInternals = false
  MapMode = 5
  Placement = pos=(0,0,32) rot=(0,0,1;0rad)
  Support = -> [Fillet]
  TreeRank = 98
  ValidateShape = true
  expr: Constraints[1] = <<Parameters>>.small_holder_diameter / 2
  sketch-geometry (1):
    g0: Circle CenterX=0 CenterY=27.875 CenterZ=0 NormalX=0 NormalY=0 NormalZ=1 AngleXU=0 Radius=0.5
  constraints (3):
    c: PointOnObject(g0,g-2)
    c: DistanceY(g-1,g0) = 27.875
    c: Diameter(g0) = 1
FEATURE [PartDesign::Pocket] Pocket015
  AddSubType = 1
  AutoTaperInnerAngle = true
  BaseFeature = -> Fillet
  CheckUpToFaceLimits = true
  ClaimChildren = false
  Fit = 0
  FitJoin = 0
  InnerFit = 0
  InnerFitJoin = 0
  InvalidShape = false
  Length = 30
  Length2 = 100
  Linearize = true
  NewSolid = false
  Profile = -> Sketch028
  Suppress = false
  TaperInnerAngle = 0
  TaperInnerAngleRev = 0
  TreeRank = 99
  Type = 0
  ValidateShape = true
  _ProfileBasedVersion = 1
  _Version = 1
  expr: Length = <<Parameters>>.shoulder_height + <<Parameters>>.cap_recess
FEATURE [PartDesign::PolarPattern] PolarPattern005
  AddSubType = 0
  Angle = 360
  Axis = -> Sketch028 [N_Axis]
  BaseFeature = -> Pocket015
  CopyShape = false
  InvalidShape = false
  NewSolid = false
  Occurrences = 32
  OriginalSubs = -> [Pocket015]
  Originals = -> [Pocket015]
  ParallelTransform = true
  SubTransform = true
  Suppress = false
  TreeRank = 100
  ValidateShape = true
  _Version = 3
FEATURE [PartDesign::Body] Body002  label="Seven Cone Cap"
  AutoGroupSolids = false
  ClaimAllChildren = false
  ExportMode = 0
  Group = -> [Sketch015,Pad002,Sketch016,Pocket009,Chamfer004,Sketch027,Helix007,Fillet,Sketch028,Pocket015,PolarPattern005]
  InvalidShape = false
  Origin = -> Origin002
  Tip = -> PolarPattern005
  TreeRank = 67
  ValidateShape = true
  _ExportChildren = -> [Pad002,Pocket009,Chamfer004,Helix007,Fillet,Pocket015,PolarPattern005]
  _GroupVersion = 1
FEATURE [PartDesign::Chamfer] Chamfer005
  AddSubType = 0
  Angle = 45
  Base = -> Pocket008 [Edge5,Edge4]
  BaseFeature = -> Pocket008
  ChamferType = 0
  FlipDirection = false
  InvalidShape = false
  NewSolid = false
  Size = 3
  Size2 = 1
  SupportTransform = false
  Suppress = false
  TreeRank = 101
  ValidateShape = true
  expr: Size = <<Parameters>>.shoulder_depth - 1
FEATURE [PartDesign::AdditiveHelix] Helix002  label="Large Top Threads"
  AddSubType = 0
  Angle = 0
  Axis = (0,0,1)
  Base = (0,0,0)
  BaseFeature = -> Chamfer005
  ClaimChildren = false
  Fit = 0
  FitJoin = 0
  Growth = 0
  HasBeenEdited = true
  Height = 12.5
  InnerFit = 0
  InnerFitJoin = 0
  InvalidShape = false
  LeftHanded = false
  Linearize = true
  Mode = 0
  NewSolid = false
  Outside = false
  Pitch = 5
  Profile = -> Sketch013
  ReferenceAxis = -> Sketch013 [V_Axis]
  Suppress = false
  TreeRank = 54
  Turns = 2.5
  ValidateShape = true
  _ProfileBasedVersion = 1
  expr: Height = <<Parameters>>.shoulder_height - <<Parameters>>.thread_pitch
  expr: Pitch = <<Parameters>>.thread_pitch * 2
FEATURE [PartDesign::AdditiveHelix] Helix003  label="Large Bottom Threads"
  AddSubType = 0
  Angle = 0
  Axis = (0,-2e-16,1)
  Base = (0,0,0)
  BaseFeature = -> Helix002
  ClaimChildren = false
  Fit = 0
  FitJoin = 0
  Growth = 0
  HasBeenEdited = true
  Height = 12.5
  InnerFit = 0
  InnerFitJoin = 0
  InvalidShape = false
  LeftHanded = false
  Linearize = true
  Mode = 0
  NewSolid = false
  Outside = false
  Pitch = 5
  Profile = -> Sketch014
  ReferenceAxis = -> Sketch014 [V_Axis]
  Suppress = false
  TreeRank = 56
  Turns = 2.5
  ValidateShape = true
  _ProfileBasedVersion = 1
  expr: Height = <<Parameters>>.shoulder_height - <<Parameters>>.thread_pitch
  expr: Pitch = <<Parameters>>.thread_pitch * 2
FEATURE [PartDesign::Chamfer] Chamfer001
  AddSubType = 0
  Angle = 45
  Base = -> Helix003 [Edge98,Edge100,Edge104,Edge118,Edge116,Edge114,Edge112,Edge96,Edge90,Edge88,Edge82,Edge80,Edge84,Edge86,Edge92,Edge94,Edge108,Edge110,Edge102,Edge106]
  BaseFeature = -> Helix003
  ChamferType = 0
  FlipDirection = false
  InvalidShape = false
  NewSolid = false
  Size = 0.6
  Size2 = 1
  SupportTransform = false
  Suppress = false
  TreeRank = 57
  ValidateShape = true
FEATURE [PartDesign::Chamfer] Chamfer003
  AddSubType = 0
  Angle = 45
  Base = -> Chamfer001 [Edge128,Edge141]
  BaseFeature = -> Chamfer001
  ChamferType = 0
  FlipDirection = false
  InvalidShape = false
  NewSolid = false
  Size = 1.75
  Size2 = 1
  SupportTransform = false
  Suppress = false
  TreeRank = 88
  ValidateShape = true
FEATURE [PartDesign::Body] Body001  label="Twenty Cone Body"
  AutoGroupSolids = false
  ClaimAllChildren = false
  ExportMode = 0
  Group = -> [Sketch003,Pad001,Sketch004,Pocket002,Sketch005,Pocket003,PolarPattern001,Sketch006,Pocket004,PolarPattern002,Sketch011,Pocket007,Sketch012,Pocket008,Chamfer005,Sketch013,Helix002,Sketch014,Helix003,Chamfer001,Chamfer003]
  InvalidShape = false
  Origin = -> Origin001
  Tip = -> Chamfer003
  TreeRank = 28
  ValidateShape = true
  _ExportChildren = -> [Pad001,Pocket002,Pocket003,PolarPattern001,Pocket004,PolarPattern002,Pocket007,Pocket008,Chamfer005,Helix002,Helix003,Chamfer001,Chamfer003]
  _GroupVersion = 1
FEATURE [PartDesign::Chamfer] Chamfer006
  AddSubType = 0
  Angle = 45
  Base = -> Pocket011 [Edge4]
  BaseFeature = -> Pocket011
  ChamferType = 0
  FlipDirection = false
  InvalidShape = false
  NewSolid = false
  Size = 3
  Size2 = 1
  SupportTransform = false
  Suppress = false
  TreeRank = 102
  ValidateShape = true
  expr: Size = <<Parameters>>.shoulder_depth - 1
FEATURE [PartDesign::SubtractiveHelix] Helix005  label="Large Cap Threads"
  AddSubType = 1
  Angle = 0
  Axis = (0,-2e-16,1)
  Base = (0,0,0)
  BaseFeature = -> Chamfer006
  ClaimChildren = false
  Fit = 0
  FitJoin = 0
  Growth = 0
  HasBeenEdited = true
  Height = 17.5
  InnerFit = 0
  InnerFitJoin = 0
  InvalidShape = false
  LeftHanded = false
  Linearize = true
  Mode = 0
  NewSolid = false
  Outside = false
  Pitch = 5
  Profile = -> Sketch022
  ReferenceAxis = -> Sketch022 [V_Axis]
  Suppress = false
  TreeRank = 76
  Turns = 3.5
  ValidateShape = true
  _ProfileBasedVersion = 1
  expr: Height = <<Parameters>>.shoulder_height + <<Parameters>>.thread_pitch
  expr: Pitch = <<Parameters>>.thread_pitch * 2
FEATURE [PartDesign::Fillet] Fillet001  label="Large Top Fillet"
  AddSubType = 0
  Base = -> Helix005 [Edge12]
  BaseFeature = -> Helix005
  InvalidShape = false
  NewSolid = false
  Radius = 5
  SupportTransform = false
  Suppress = false
  TreeRank = 77
  ValidateShape = true
FEATURE [Sketcher::SketchObject] Sketch024
  ArcFitTolerance = 1e-06
  AttachmentSupport = -> [Fillet001]
  ExternalBSplineMaxDegree = 5
  ExternalBSplineTolerance = 0.0001
  FullyConstrained = true
  InternalTolerance = 1e-06
  InvalidShape = false
  MakeInternals = false
  MapMode = 5
  Placement = pos=(0,0,0) rot=(1,0,0;3.14159rad)
  Support = -> [Fillet001]
  TreeRank = 82
  ValidateShape = true
  expr: Constraints[1] = <<Parameters>>.large_holder_diameter / 2
  sketch-geometry (1):
    g0: Circle CenterX=0 CenterY=43.125 CenterZ=0 NormalX=0 NormalY=0 NormalZ=1 AngleXU=0 Radius=0.5
  constraints (3):
    c: PointOnObject(g0,g-2)
    c: DistanceY(g-1,g0) = 43.125
    c: Diameter(g0) = 1
FEATURE [PartDesign::Pocket] Pocket014  label="Large Grip"
  AddSubType = 1
  AutoTaperInnerAngle = true
  BaseFeature = -> Fillet001
  CheckUpToFaceLimits = true
  ClaimChildren = false
  Fit = 0
  FitJoin = 0
  InnerFit = 0
  InnerFitJoin = 0
  InvalidShape = false
  Length = 26
  Length2 = 100
  Linearize = true
  NewSolid = false
  Profile = -> Sketch024
  Suppress = false
  TaperInnerAngle = 0
  TaperInnerAngleRev = 0
  TreeRank = 83
  Type = 0
  ValidateShape = true
  _ProfileBasedVersion = 1
  _Version = 1
  expr: Length = <<Parameters>>.shoulder_height + <<Parameters>>.cap_recess - 2 * <<Parameters>>.Thickness
FEATURE [PartDesign::PolarPattern] PolarPattern004  label="Large Grip Ring"
  AddSubType = 0
  Angle = 360
  Axis = -> Sketch024 [N_Axis]
  BaseFeature = -> Pocket014
  CopyShape = false
  InvalidShape = false
  NewSolid = false
  Occurrences = 55
  OriginalSubs = -> [Pocket014]
  Originals = -> [Pocket014]
  ParallelTransform = true
  SubTransform = true
  Suppress = false
  TreeRank = 84
  ValidateShape = true
  _Version = 3
  expr: Occurrences = floor(36 * 1.55)
FEATURE [PartDesign::Body] Body003  label="Twenty Cone Cap"
  AutoGroupSolids = false
  ClaimAllChildren = false
  ExportMode = 0
  Group = -> [Sketch019,Pad003,Sketch020,Pocket011,Chamfer006,Sketch022,Helix005,Fillet001,Sketch024,Pocket014,PolarPattern004]
  InvalidShape = false
  Origin = -> Origin003
  Tip = -> PolarPattern004
  TreeRank = 78
  ValidateShape = true
  _ExportChildren = -> [Pad003,Pocket011,Chamfer006,Helix005,Fillet001,Pocket014,PolarPattern004]
  _GroupVersion = 1
